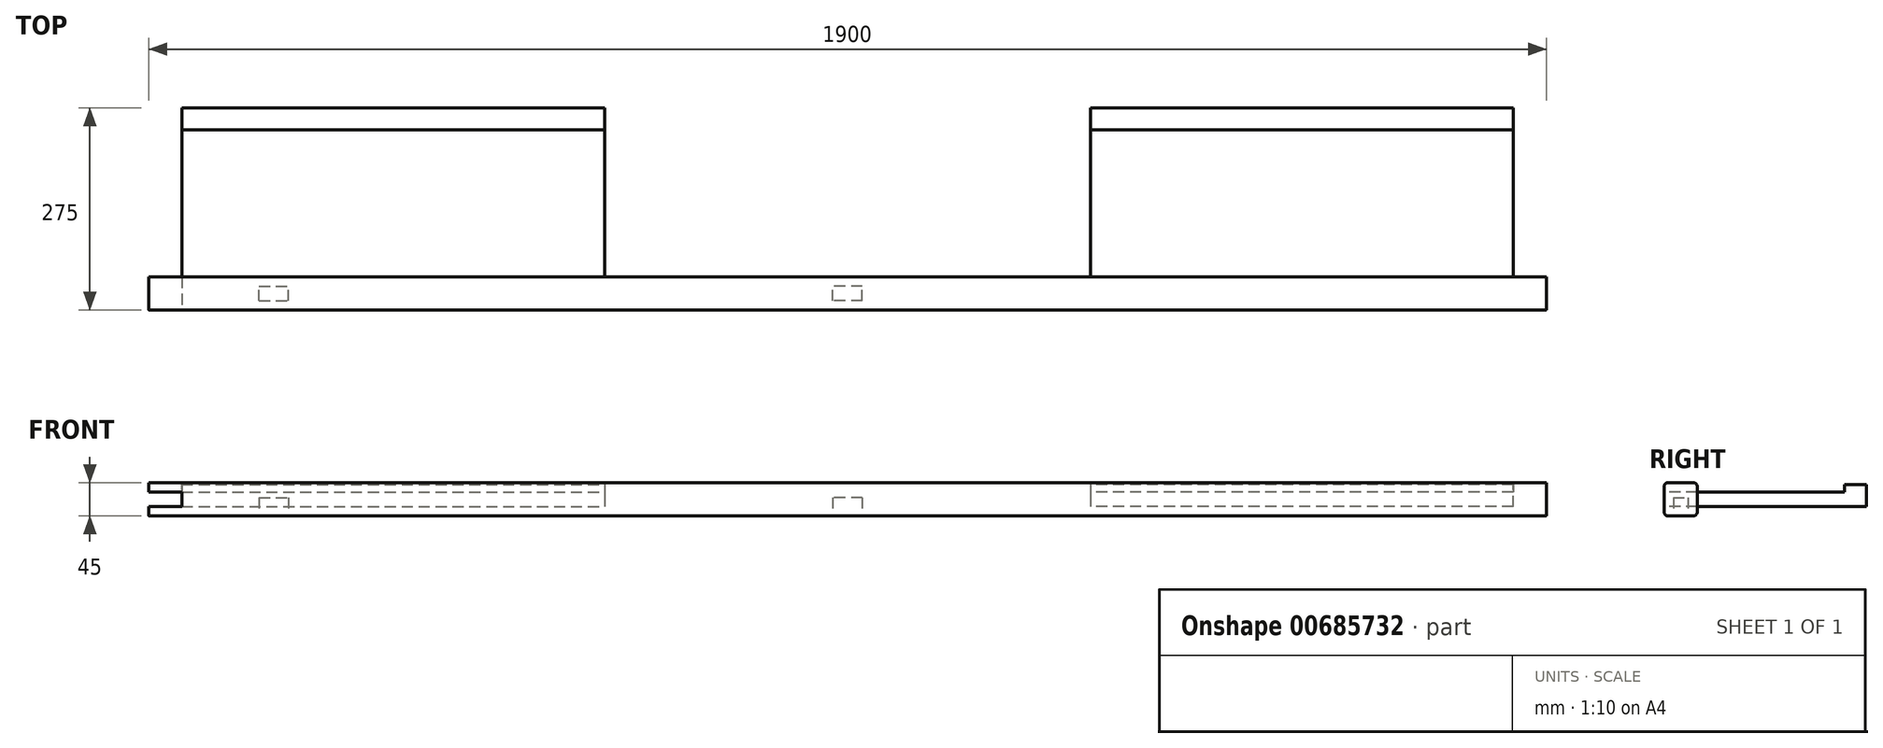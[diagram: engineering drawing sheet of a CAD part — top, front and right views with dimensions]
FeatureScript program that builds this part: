
annotation { "Feature Type Name" : "Feature", "Feature Type Description" : "" }
export const myFeature = defineFeature(function(context is Context, id is Id, definition is map)
    precondition{}
    {
        {
            var Q0;
            Q0=qCreatedBy(makeId("Right.planeOp"),FACE);
            var sketch = newSketch(context, id + "F0", { "sketchPlane" : qUnion([Q0])});
            skLineSegment(sketch, "E0.bottom", {"start": v(0, 0) * mm, "end": v(45, 0) * mm});
            skLineSegment(sketch, "E0.top", {"start": v(0, 45) * mm, "end": v(45, 45) * mm});
            skLineSegment(sketch, "E0.left", {"start": v(0, 0) * mm, "end": v(0, 45) * mm});
            skLineSegment(sketch, "E0.right", {"start": v(45, 0) * mm, "end": v(45, 45) * mm});
            skSolve(sketch);
        }
        {
            var Q0;
            Q0=qSketchRegion(id+"F0",true);
            extrude(context, id + "F1", {"entities" : qUnion([Q0]), "endBound" : BoundingType.SYMMETRIC, "depth" : 1900 * mm, "offsetDistance" : 25 * mm});
        }
        {
            var Q0;
            Q0=makeQuery(id+"F1.opExtrude","SWEPT_EDGE",EDGE,{"disambiguationData":[OSD([sQuery(id+"F0.wireOp",EDGE,"E0.top"),sQuery(id+"F0.wireOp",EDGE,"E0.left")])]});
            var Q1;
            Q1=makeQuery(id+"F1.opExtrude","SWEPT_EDGE",EDGE,{"disambiguationData":[OSD([sQuery(id+"F0.wireOp",EDGE,"E0.top"),sQuery(id+"F0.wireOp",EDGE,"E0.right")])]});
            var Q2;
            Q2=makeQuery(id+"F1.opExtrude","SWEPT_EDGE",EDGE,{"disambiguationData":[OSD([sQuery(id+"F0.wireOp",EDGE,"E0.bottom"),sQuery(id+"F0.wireOp",EDGE,"E0.left")])]});
            var Q3;
            Q3=makeQuery(id+"F1.opExtrude","SWEPT_EDGE",EDGE,{"disambiguationData":[OSD([sQuery(id+"F0.wireOp",EDGE,"E0.bottom"),sQuery(id+"F0.wireOp",EDGE,"E0.right")])]});
            fillet(context, id + "F2", {"entities" : qUnion([Q0, Q1, Q2, Q3]), "radius" : 5 * mm, "tangentPropagation" : true, "allowEdgeOverflow" : false});
        }
        {
            var Q0;
            Q0=makeQuery(id+"F1.opExtrude","SWEPT_FACE",FACE,{"disambiguationData":[OSD([sQuery(id+"F0.wireOp",EDGE,"E0.left")])]});
            var sketch = newSketch(context, id + "F3", { "sketchPlane" : qUnion([Q0])});
            skLineSegment(sketch, "E1", {"start": v(-950, 22.5) * mm, "end": v(-905, 22.5) * mm, "construction": true});
            skLineSegment(sketch, "E2.bottom", {"start": v(-905, 12.5) * mm, "end": v(-950, 12.5) * mm});
            skLineSegment(sketch, "E2.top", {"start": v(-905, 32.5) * mm, "end": v(-950, 32.5) * mm});
            skLineSegment(sketch, "E2.left", {"start": v(-905, 12.5) * mm, "end": v(-905, 32.5) * mm});
            skLineSegment(sketch, "E2.right", {"start": v(-950, 12.5) * mm, "end": v(-950, 32.5) * mm});
            skPoint(sketch, "E2.middle", {"position": v(-927.5, 22.5) * mm});
            skSolve(sketch);
        }
        {
            var Q0;
            Q0=qSketchRegion(id+"F3",true);
            extrude(context, id + "F4", {"entities" : qUnion([Q0]), "operationType" : NewBodyOperationType.REMOVE, "endBound" : BoundingType.THROUGH_ALL, "oppositeDirection" : true, "depth" : 25 * mm, "offsetDistance" : 25 * mm});
        }
        {
            var Q0;
            Q0=makeQuery(id+"F1.opExtrude","SWEPT_FACE",FACE,{"disambiguationData":[OSD([sQuery(id+"F0.wireOp",EDGE,"E0.bottom")])]});
            var sketch = newSketch(context, id + "F5", { "sketchPlane" : qUnion([Q0])});
            skLineSegment(sketch, "E3.bottom", {"start": v(-800, -12.5) * mm, "end": v(-760, -12.5) * mm});
            skLineSegment(sketch, "E3.top", {"start": v(-800, -32.5) * mm, "end": v(-760, -32.5) * mm});
            skLineSegment(sketch, "E3.left", {"start": v(-800, -12.5) * mm, "end": v(-800, -32.5) * mm});
            skLineSegment(sketch, "E3.right", {"start": v(-760, -12.5) * mm, "end": v(-760, -32.5) * mm});
            skPoint(sketch, "E3.middle", {"position": v(-780, -22.5) * mm});
            skPoint(sketch, "E3.middle.positionSnap0", {"position": v(-950, -22.5) * mm});
            skPoint(sketch, "E3.centerSnap0", {"position": v(-950, -22.5) * mm});
            skSolve(sketch);
        }
        {
            var Q0;
            Q0=qSketchRegion(id+"F5",true);
            extrude(context, id + "F6", {"entities" : qUnion([Q0]), "operationType" : NewBodyOperationType.REMOVE, "oppositeDirection" : true, "depth" : 25 * mm, "offsetDistance" : 25 * mm});
        }
        {
            var Q0;
            Q0=makeQuery(id+"F1.opExtrude","SWEPT_FACE",FACE,{"disambiguationData":[OSD([sQuery(id+"F0.wireOp",EDGE,"E0.bottom")])]});
            var sketch = newSketch(context, id + "F7", { "sketchPlane" : qUnion([Q0])});
            skLineSegment(sketch, "E4.bottom", {"start": v(20, -12.5) * mm, "end": v(-20, -12.5) * mm});
            skLineSegment(sketch, "E4.top", {"start": v(20, -32.5) * mm, "end": v(-20, -32.5) * mm});
            skLineSegment(sketch, "E4.left", {"start": v(20, -12.5) * mm, "end": v(20, -32.5) * mm});
            skLineSegment(sketch, "E4.right", {"start": v(-20, -12.5) * mm, "end": v(-20, -32.5) * mm});
            skPoint(sketch, "E4.middle", {"position": v(0, -22.5) * mm});
            skLineSegment(sketch, "E5", {"start": v(950, -22.5) * mm, "end": v(-950, -22.5) * mm, "construction": true});
            skSolve(sketch);
        }
        {
            var Q0;
            Q0=qSketchRegion(id+"F7",true);
            extrude(context, id + "F8", {"entities" : qUnion([Q0]), "operationType" : NewBodyOperationType.REMOVE, "oppositeDirection" : true, "depth" : 25 * mm, "offsetDistance" : 25 * mm});
        }
        {
            var Q0;
            Q0=makeQuery(id+"F1.opExtrude","SWEPT_FACE",FACE,{"disambiguationData":[OSD([sQuery(id+"F0.wireOp",EDGE,"E0.right")])]});
            var sketch = newSketch(context, id + "F9", { "sketchPlane" : qUnion([Q0])});
            skLineSegment(sketch, "E6", {"start": v(-905, 12.5) * mm, "end": v(-330, 12.5) * mm});
            skLineSegment(sketch, "E7", {"start": v(-905, 32.5) * mm, "end": v(-330, 32.5) * mm});
            skLineSegment(sketch, "E8", {"start": v(-330, 32.5) * mm, "end": v(-330, 12.5) * mm});
            skLineSegment(sketch, "E9", {"start": v(-905, 12.5) * mm, "end": v(-905, 32.5) * mm});
            skLineSegment(sketch, "E10", {"start": v(0, 0) * mm, "end": v(0, 31.33) * mm});
            skPoint(sketch, "E10.endSnap0", {"position": v(0, 5) * mm});
            skLineSegment(sketch, "E11.MirrorCS", {"start": v(905, 32.5) * mm, "end": v(330, 32.5) * mm});
            skLineSegment(sketch, "E12.MirrorCS", {"start": v(330, 32.5) * mm, "end": v(330, 12.5) * mm});
            skLineSegment(sketch, "E13.MirrorCS", {"start": v(905, 12.5) * mm, "end": v(330, 12.5) * mm});
            skLineSegment(sketch, "E14.MirrorCS", {"start": v(905, 12.5) * mm, "end": v(905, 32.5) * mm});
            skSolve(sketch);
        }
        {
            var Q0;
            Q0 = qSketchRegion(id + "F9", true);
            extrude(context, id + "F10", {"entities" : qUnion([Q0]), "operationType" : NewBodyOperationType.ADD, "depth" : 230 * mm, "offsetDistance" : 25 * mm});
        }
        {
            var Q0;
            Q0=makeQuery(id+"F10.opExtrude","SWEPT_FACE",FACE,{"disambiguationData":[OSD([sQuery(id+"F9.wireOp",EDGE,"E11.MirrorCS")])]});
            var sketch = newSketch(context, id + "F11", { "sketchPlane" : qUnion([Q0])});
            skLineSegment(sketch, "E15.bottom", {"start": v(-905, 275) * mm, "end": v(-330, 275) * mm});
            skLineSegment(sketch, "E15.top", {"start": v(-905, 245) * mm, "end": v(-330, 245) * mm});
            skLineSegment(sketch, "E15.left", {"start": v(-905, 275) * mm, "end": v(-905, 245) * mm});
            skLineSegment(sketch, "E15.right", {"start": v(-330, 275) * mm, "end": v(-330, 245) * mm});
            skLineSegment(sketch, "E16", {"start": v(0, 0) * mm, "end": v(0, 46.75) * mm});
            skLineSegment(sketch, "E17.MirrorCS", {"start": v(905, 275) * mm, "end": v(905, 245) * mm});
            skLineSegment(sketch, "E18.MirrorCS", {"start": v(330, 275) * mm, "end": v(330, 245) * mm});
            skLineSegment(sketch, "E19.MirrorCS", {"start": v(905, 275) * mm, "end": v(330, 275) * mm});
            skLineSegment(sketch, "E20.MirrorCS", {"start": v(905, 245) * mm, "end": v(330, 245) * mm});
            skSolve(sketch);
        }
        {
            var Q0;
            Q0 = qSketchRegion(id + "F11", true);
            extrude(context, id + "F12", {"entities" : qUnion([Q0]), "operationType" : NewBodyOperationType.ADD, "depth" : 10 * mm, "offsetDistance" : 25 * mm});
        }
    });
